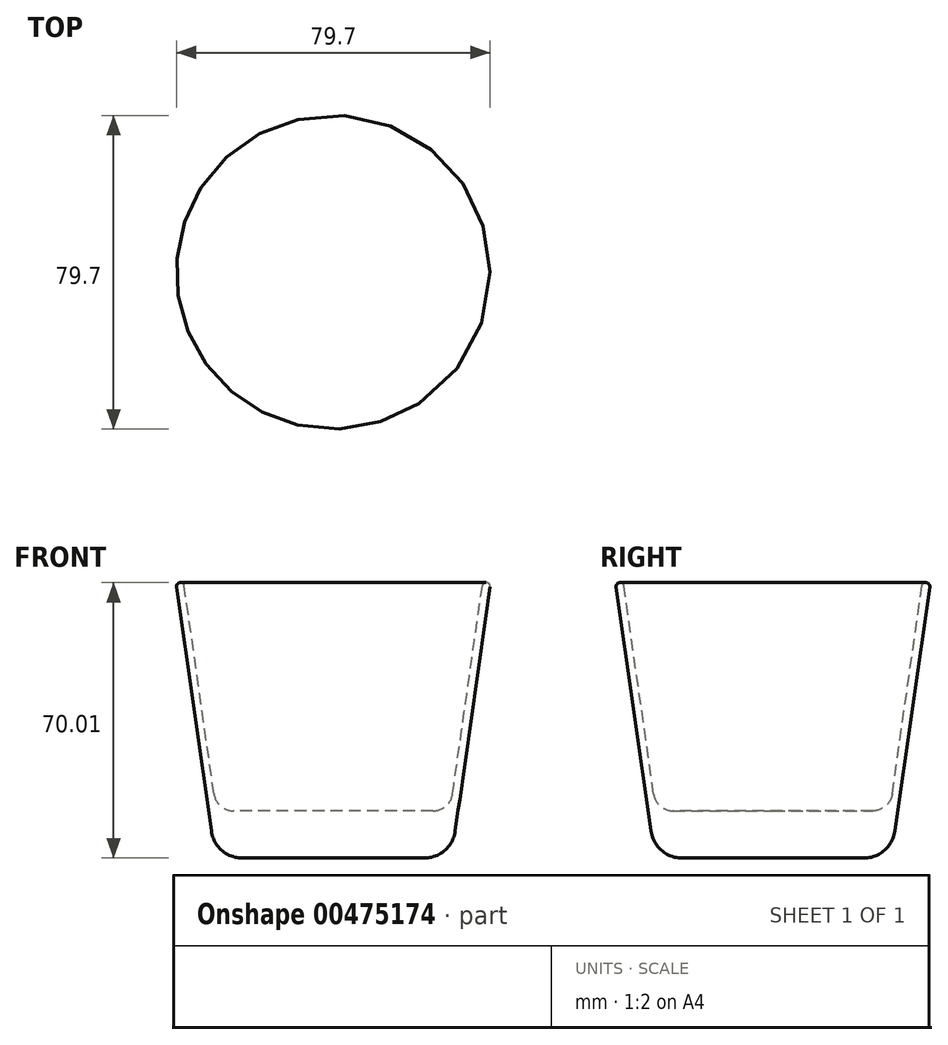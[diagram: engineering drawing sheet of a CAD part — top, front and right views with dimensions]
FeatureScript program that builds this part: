
annotation { "Feature Type Name" : "Feature", "Feature Type Description" : "" }
export const myFeature = defineFeature(function(context is Context, id is Id, definition is map)
    precondition{}
    {
        {
            var Q0;
            Q0=qCreatedBy(makeId("Front.planeOp"),FACE);
            var sketch = newSketch(context, id + "F0", { "sketchPlane" : qUnion([Q0])});
            skLineSegment(sketch, "E0", {"start": v(0, 81.94) * mm, "end": v(0, 0) * mm, "construction": true});
            skLineSegment(sketch, "E1", {"start": v(0, 0) * mm, "end": v(23.06, 0) * mm});
            skLineSegment(sketch, "E2", {"start": v(39.84, 68.87) * mm, "end": v(30.98, 6.87) * mm});
            skPoint(sketch, "E3.visualSharp", {"position": v(30, 0) * mm});
            skArc(sketch, "E3.filletArc", {"start": v(23.06, 0) * mm, "mid": v(28.3, 1.96) * mm, "end": v(30.98, 6.87) * mm});
            skLineSegment(sketch, "E4.2", {"start": v(37.86, 69.15) * mm, "end": v(30.3, 16.3) * mm});
            skLineSegment(sketch, "E5.0", {"start": v(0, 12) * mm, "end": v(25.36, 12) * mm});
            skArc(sketch, "E6.filletArc", {"start": v(25.36, 12) * mm, "mid": v(28.63, 13.22) * mm, "end": v(30.3, 16.3) * mm});
            skArc(sketch, "E7", {"start": v(39.84, 68.87) * mm, "mid": v(38.99, 70) * mm, "end": v(37.86, 69.15) * mm});
            skPoint(sketch, "E7.first.point", {"position": v(37.86, 69.15) * mm});
            skPoint(sketch, "E7.second.point", {"position": v(38.99, 70) * mm});
            skPoint(sketch, "E7.third.point", {"position": v(39.84, 68.87) * mm});
            skPoint(sketch, "E8.orphan", {"position": v(37.98, 70) * mm});
            skPoint(sketch, "E9.orphan", {"position": v(40, 70) * mm});
            skLineSegment(sketch, "E10", {"start": v(0, 12) * mm, "end": v(0, 0) * mm});
            skSolve(sketch);
        }
        {
            var Q0;
            Q0=makeQuery(id+"F0.imprint","IMPRINT",FACE,{"disambiguationData":[TD([[makeQuery(id+"F0.imprint","IMPRINT",EDGE,{"derivedFrom":sQuery(id+"F0.wireOp",EDGE,"E1")}),1.0]])]});
            var Q1;
            Q1=sQuery(id+"F0.wireOp",EDGE,"E10");
            revolve(context, id + "F1", {"entities" : qUnion([Q0]), "axis" : qUnion([Q1]), "revolveType" : RevolveType.FULL});
        }
    });
